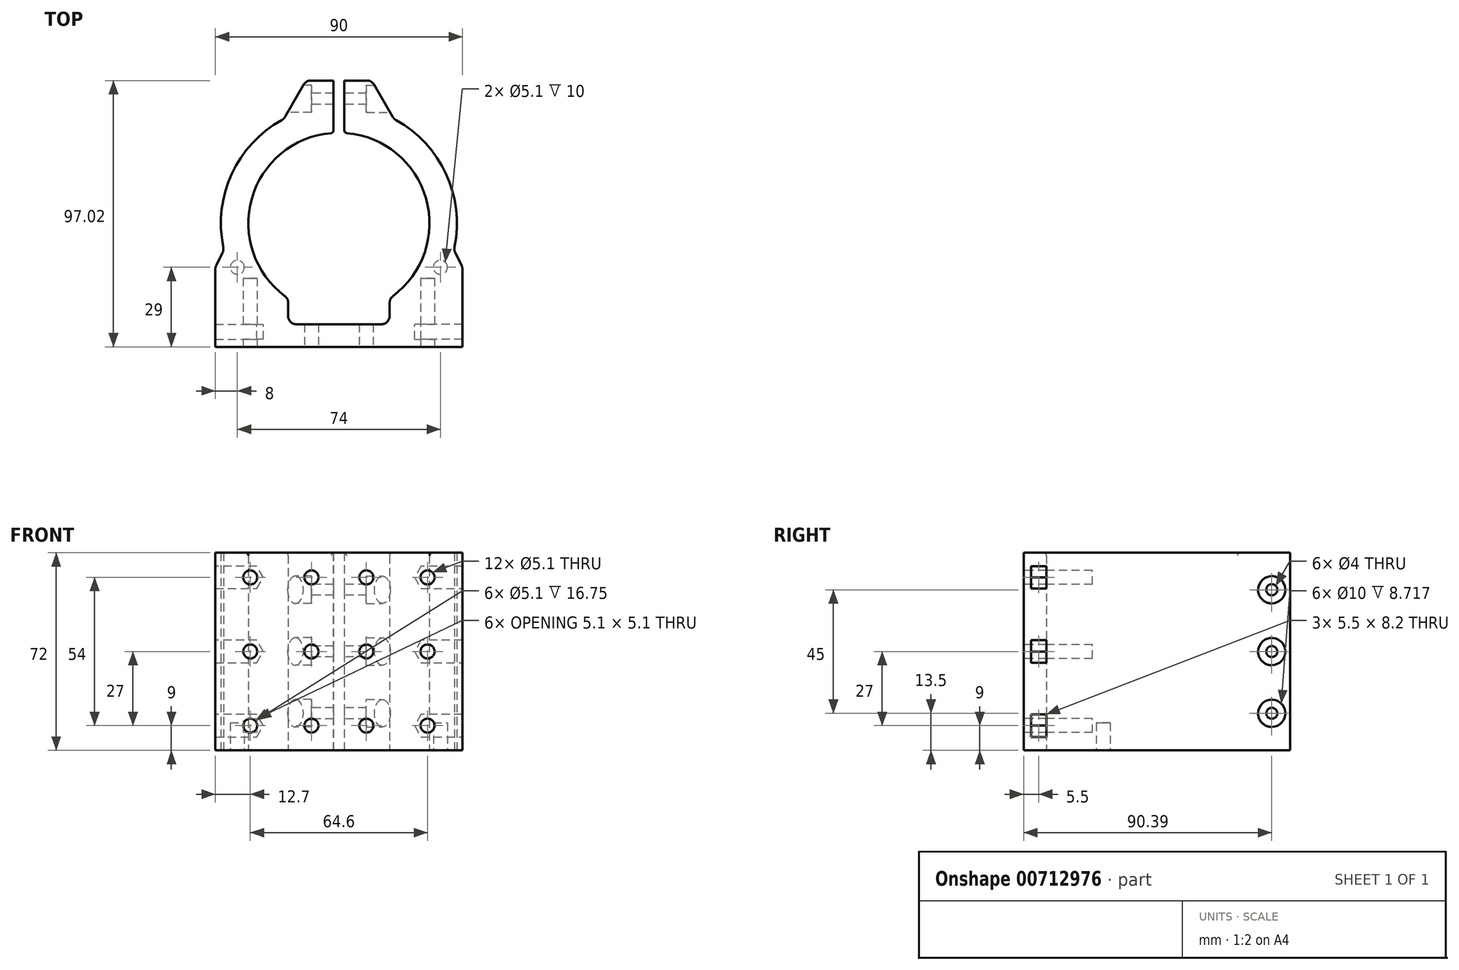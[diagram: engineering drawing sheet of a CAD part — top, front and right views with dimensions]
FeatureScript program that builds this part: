
annotation { "Feature Type Name" : "Feature", "Feature Type Description" : "" }
export const myFeature = defineFeature(function(context is Context, id is Id, definition is map)
    precondition{}
    {
        {
            var Q0;
            Q0=qCreatedBy(makeId("Top.planeOp"),FACE);
            var sketch = newSketch(context, id + "F0", { "sketchPlane" : qUnion([Q0])});
            skLineSegment(sketch, "E0", {"start": v(-45, -16) * mm, "end": v(-45, -45) * mm});
            skLineSegment(sketch, "E1", {"start": v(-45, -45) * mm, "end": v(45, -45) * mm});
            skLineSegment(sketch, "E2", {"start": v(45, -45) * mm, "end": v(45, -16) * mm});
            skLineSegment(sketch, "E3", {"start": v(45, -16) * mm, "end": v(41.9, -9.67) * mm});
            skLineSegment(sketch, "E4", {"start": v(-45, -16) * mm, "end": v(-41.9, -9.67) * mm});
            skLineSegment(sketch, "E5", {"start": v(-18.5, -27.33) * mm, "end": v(-18.5, -36.75) * mm});
            skLineSegment(sketch, "E6", {"start": v(-18.5, -36.75) * mm, "end": v(18.5, -36.75) * mm});
            skLineSegment(sketch, "E7", {"start": v(18.5, -36.75) * mm, "end": v(18.5, -27.33) * mm});
            skArc(sketch, "E8", {"start": v(-18.5, -27.33) * mm, "mid": v(-31.83, 8.71) * mm, "end": v(-2, 32.94) * mm});
            skArc(sketch, "E9", {"start": v(2, 32.94) * mm, "mid": v(31.83, 8.71) * mm, "end": v(18.5, -27.33) * mm});
            skArc(sketch, "E10", {"start": v(-41.9, -9.67) * mm, "mid": v(-39.1, 17.88) * mm, "end": v(-20.08, 38.02) * mm});
            skArc(sketch, "E11", {"start": v(20.08, 38.02) * mm, "mid": v(39.1, 17.88) * mm, "end": v(41.9, -9.67) * mm});
            skCircle(sketch, "E12", {"center": v(-37, -16) * mm, "radius": 2.55 * mm, "construction": true});
            skLineSegment(sketch, "E13", {"start": v(-37, -16) * mm, "end": v(-45, -16) * mm, "construction": true});
            skLineSegment(sketch, "E14", {"start": v(-37, -16) * mm, "end": v(-41.9, -9.67) * mm, "construction": true});
            skCircle(sketch, "E15", {"center": v(37, -16) * mm, "radius": 2.55 * mm, "construction": true});
            skLineSegment(sketch, "E16", {"start": v(37, -16) * mm, "end": v(41.9, -9.67) * mm, "construction": true});
            skLineSegment(sketch, "E17", {"start": v(37, -16) * mm, "end": v(45, -16) * mm, "construction": true});
            skLineSegment(sketch, "E18", {"start": v(-2, 32.94) * mm, "end": v(-2, 52.02) * mm});
            skLineSegment(sketch, "E19", {"start": v(2, 32.94) * mm, "end": v(2, 52.02) * mm});
            skLineSegment(sketch, "E20", {"start": v(2, 52.02) * mm, "end": v(12, 52.02) * mm});
            skLineSegment(sketch, "E21", {"start": v(12, 52.02) * mm, "end": v(20.08, 38.02) * mm});
            skLineSegment(sketch, "E22", {"start": v(-2, 52.02) * mm, "end": v(-12, 52.02) * mm});
            skLineSegment(sketch, "E23", {"start": v(-12, 52.02) * mm, "end": v(-20.08, 38.02) * mm});
            skLineSegment(sketch, "E24", {"start": v(-16.04, 45.02) * mm, "end": v(16.04, 45.02) * mm, "construction": true});
            skPoint(sketch, "E25", {"position": v(-2, 45.02) * mm});
            skSolve(sketch);
        }
        {
            var Q0;
            Q0 = qSketchRegion(id + "F0", true);
            extrude(context, id + "F1", {"entities" : qUnion([Q0]), "depth" : (18 * 4) * mm, "offsetDistance" : 25 * mm});
        }
        {
            var Q0;
            Q0=makeQuery(id+"F1.opExtrude","SWEPT_FACE",FACE,{"disambiguationData":[OSD([sQuery(id+"F0.wireOp",EDGE,"E1")])]});
            var sketch = newSketch(context, id + "F2", { "sketchPlane" : qUnion([Q0])});
            skCircle(sketch, "E26", {"center": v(-32.3, 9) * mm, "radius": 2.55 * mm});
            skCircle(sketch, "E27", {"center": v(-10, 9) * mm, "radius": 2.55 * mm});
            skCircle(sketch, "E28", {"center": v(10, 9) * mm, "radius": 2.55 * mm});
            skCircle(sketch, "E29", {"center": v(32.3, 9) * mm, "radius": 2.55 * mm});
            skCircle(sketch, "E30", {"center": v(32.3, 36) * mm, "radius": 2.55 * mm});
            skCircle(sketch, "E31", {"center": v(10, 36) * mm, "radius": 2.55 * mm});
            skCircle(sketch, "E32", {"center": v(-10, 36) * mm, "radius": 2.55 * mm});
            skCircle(sketch, "E33", {"center": v(-32.3, 36) * mm, "radius": 2.55 * mm});
            skCircle(sketch, "E34", {"center": v(-32.3, 63) * mm, "radius": 2.55 * mm});
            skCircle(sketch, "E35", {"center": v(-10, 63) * mm, "radius": 2.55 * mm});
            skCircle(sketch, "E36", {"center": v(10, 63) * mm, "radius": 2.55 * mm});
            skCircle(sketch, "E37", {"center": v(32.3, 63) * mm, "radius": 2.55 * mm});
            skLineSegment(sketch, "E38", {"start": v(-45, 9) * mm, "end": v(45, 9) * mm, "construction": true});
            skLineSegment(sketch, "E39", {"start": v(-45, 36) * mm, "end": v(45, 36) * mm, "construction": true});
            skLineSegment(sketch, "E40", {"start": v(-45, 63) * mm, "end": v(45, 63) * mm, "construction": true});
            skLineSegment(sketch, "E41", {"start": v(-32.3, 72) * mm, "end": v(-32.3, 0) * mm, "construction": true});
            skLineSegment(sketch, "E42", {"start": v(-10, 72) * mm, "end": v(-10, 0) * mm, "construction": true});
            skLineSegment(sketch, "E43", {"start": v(10, 72) * mm, "end": v(10, 0) * mm, "construction": true});
            skLineSegment(sketch, "E44", {"start": v(32.3, 72) * mm, "end": v(32.3, 0) * mm, "construction": true});
            skSolve(sketch);
        }
        {
            var Q0;
            Q0 = qSketchRegion(id + "F2", true);
            extrude(context, id + "F3", {"entities" : qUnion([Q0]), "operationType" : NewBodyOperationType.REMOVE, "oppositeDirection" : true, "depth" : 25 * mm, "offsetDistance" : 25 * mm});
        }
        {
            var Q0;
            Q0=makeQuery(id+"F1.opExtrude","CAP_FACE",FACE,{"disambiguationData":[OSD([sQuery(id+"F0.wireOp",EDGE,"E0"),sQuery(id+"F0.wireOp",EDGE,"E1"),sQuery(id+"F0.wireOp",EDGE,"E2"),sQuery(id+"F0.wireOp",EDGE,"E3"),sQuery(id+"F0.wireOp",EDGE,"E4"),sQuery(id+"F0.wireOp",EDGE,"E5"),sQuery(id+"F0.wireOp",EDGE,"E6"),sQuery(id+"F0.wireOp",EDGE,"E7"),sQuery(id+"F0.wireOp",EDGE,"E8"),sQuery(id+"F0.wireOp",EDGE,"E9"),sQuery(id+"F0.wireOp",EDGE,"E10"),sQuery(id+"F0.wireOp",EDGE,"E11"),sQuery(id+"F0.wireOp",EDGE,"E18"),sQuery(id+"F0.wireOp",EDGE,"E19"),sQuery(id+"F0.wireOp",EDGE,"E20"),sQuery(id+"F0.wireOp",EDGE,"E21"),sQuery(id+"F0.wireOp",EDGE,"E22"),sQuery(id+"F0.wireOp",EDGE,"E23")])],"isStart":true});
            var sketch = newSketch(context, id + "F4", { "sketchPlane" : qUnion([Q0])});
            skCircle(sketch, "E45", {"center": v(-37, 16) * mm, "radius": 2.55 * mm});
            skCircle(sketch, "E46", {"center": v(37, 16) * mm, "radius": 2.55 * mm});
            skSolve(sketch);
        }
        {
            var Q0;
            Q0 = qSketchRegion(id + "F4", true);
            extrude(context, id + "F5", {"entities" : qUnion([Q0]), "operationType" : NewBodyOperationType.REMOVE, "oppositeDirection" : true, "depth" : 10 * mm, "offsetDistance" : 25 * mm});
        }
        {
            var Q0;
            Q0=makeQuery(id+"F1.opExtrude","SWEPT_EDGE",EDGE,{"disambiguationData":[OSD([sQuery(id+"F0.wireOp",EDGE,"E7"),sQuery(id+"F0.wireOp",EDGE,"E9")])]});
            var Q1;
            Q1=makeQuery(id+"F1.opExtrude","SWEPT_EDGE",EDGE,{"disambiguationData":[OSD([sQuery(id+"F0.wireOp",EDGE,"E6"),sQuery(id+"F0.wireOp",EDGE,"E7")])]});
            var Q2;
            Q2=makeQuery(id+"F1.opExtrude","SWEPT_EDGE",EDGE,{"disambiguationData":[OSD([sQuery(id+"F0.wireOp",EDGE,"E5"),sQuery(id+"F0.wireOp",EDGE,"E8")])]});
            var Q3;
            Q3=makeQuery(id+"F1.opExtrude","SWEPT_EDGE",EDGE,{"disambiguationData":[OSD([sQuery(id+"F0.wireOp",EDGE,"E5"),sQuery(id+"F0.wireOp",EDGE,"E6")])]});
            fillet(context, id + "F6", {"entities" : qUnion([Q0, Q1, Q2, Q3]), "radius" : 3 * mm, "tangentPropagation" : true, "allowEdgeOverflow" : false});
        }
        {
            var Q0;
            Q0=makeQuery(id+"F1.opExtrude","SWEPT_EDGE",EDGE,{"disambiguationData":[OSD([sQuery(id+"F0.wireOp",EDGE,"E4"),sQuery(id+"F0.wireOp",EDGE,"E10")])]});
            var Q1;
            Q1=makeQuery(id+"F1.opExtrude","SWEPT_EDGE",EDGE,{"disambiguationData":[OSD([sQuery(id+"F0.wireOp",EDGE,"E0"),sQuery(id+"F0.wireOp",EDGE,"E4")])]});
            var Q2;
            Q2=makeQuery(id+"F1.opExtrude","SWEPT_EDGE",EDGE,{"disambiguationData":[OSD([sQuery(id+"F0.wireOp",EDGE,"E3"),sQuery(id+"F0.wireOp",EDGE,"E11")])]});
            var Q3;
            Q3=makeQuery(id+"F1.opExtrude","SWEPT_EDGE",EDGE,{"disambiguationData":[OSD([sQuery(id+"F0.wireOp",EDGE,"E2"),sQuery(id+"F0.wireOp",EDGE,"E3")])]});
            fillet(context, id + "F7", {"entities" : qUnion([Q0, Q1, Q2, Q3]), "radius" : 3 * mm, "tangentPropagation" : true, "allowEdgeOverflow" : false});
        }
        {
            var Q0;
            Q0=makeQuery(id+"F1.opExtrude","SWEPT_EDGE",EDGE,{"disambiguationData":[OSD([sQuery(id+"F0.wireOp",EDGE,"E10"),sQuery(id+"F0.wireOp",EDGE,"E23")])]});
            var Q1;
            Q1=makeQuery(id+"F1.opExtrude","SWEPT_EDGE",EDGE,{"disambiguationData":[OSD([sQuery(id+"F0.wireOp",EDGE,"E11"),sQuery(id+"F0.wireOp",EDGE,"E21")])]});
            fillet(context, id + "F8", {"entities" : qUnion([Q0, Q1]), "radius" : 3 * mm, "tangentPropagation" : true, "allowEdgeOverflow" : false});
        }
        {
            var Q0;
            Q0=qCreatedBy(makeId("Right.planeOp"),FACE);
            var sketch = newSketch(context, id + "F9", { "sketchPlane" : qUnion([Q0])});
            skLineSegment(sketch, "E47", {"start": v(52.02, 36) * mm, "end": v(-45, 36) * mm, "construction": true});
            skLineSegment(sketch, "E48", {"start": v(60.74, 58.5) * mm, "end": v(-53.65, 58.5) * mm, "construction": true});
            skLineSegment(sketch, "E49", {"start": v(60, 13.5) * mm, "end": v(-56.08, 13.5) * mm, "construction": true});
            skLineSegment(sketch, "E50", {"start": v(45.39, 72) * mm, "end": v(45.39, 0) * mm, "construction": true});
            skCircle(sketch, "E51", {"center": v(45.39, 58.5) * mm, "radius": 2 * mm});
            skCircle(sketch, "E52", {"center": v(45.39, 36) * mm, "radius": 2 * mm});
            skCircle(sketch, "E53", {"center": v(45.39, 13.5) * mm, "radius": 2 * mm});
            skSolve(sketch);
        }
        {
            var Q0;
            Q0 = qSketchRegion(id + "F9", true);
            extrude(context, id + "F10", {"entities" : qUnion([Q0]), "operationType" : NewBodyOperationType.REMOVE, "depth" : 25 * mm, "offsetDistance" : 25 * mm, "hasSecondDirection" : true, "secondDirectionOppositeDirection" : true, "secondDirectionDepth" : 25 * mm});
        }
        {
            var Q0;
            Q0=qCreatedBy(makeId("Right.planeOp"),FACE);
            cPlane(context, id + "F11", {"entities" : qUnion([Q0]), "cplaneType" : CPlaneType.OFFSET, "offset" : 25 * mm, "width" : 150 * mm, "height" : 150 * mm});
        }
        {
            var Q0;
            Q0=qCreatedBy(makeId("Right.planeOp"),FACE);
            cPlane(context, id + "F12", {"entities" : qUnion([Q0]), "cplaneType" : CPlaneType.OFFSET, "offset" : 25 * mm, "oppositeDirection" : true, "width" : 150 * mm, "height" : 150 * mm});
        }
        {
            var Q0;
            Q0=qCreatedBy(id+"F11.planeOp",FACE);
            var sketch = newSketch(context, id + "F13", { "sketchPlane" : qUnion([Q0])});
            skCircle(sketch, "E54.0", {"center": v(45.39, 58.5) * mm, "radius": 2 * mm, "construction": true});
            skCircle(sketch, "E55.0", {"center": v(45.39, 36) * mm, "radius": 2 * mm, "construction": true});
            skCircle(sketch, "E56.0", {"center": v(45.39, 13.5) * mm, "radius": 2 * mm, "construction": true});
            skCircle(sketch, "E57", {"center": v(45.39, 58.5) * mm, "radius": 5 * mm});
            skCircle(sketch, "E58", {"center": v(45.39, 36) * mm, "radius": 5 * mm});
            skCircle(sketch, "E59", {"center": v(45.39, 13.5) * mm, "radius": 5 * mm});
            skSolve(sketch);
        }
        {
            var Q0;
            Q0 = qSketchRegion(id + "F13", true);
            extrude(context, id + "F14", {"entities" : qUnion([Q0]), "operationType" : NewBodyOperationType.REMOVE, "oppositeDirection" : true, "depth" : 15 * mm, "offsetDistance" : 25 * mm});
        }
        {
            var Q0;
            Q0=qCreatedBy(id+"F12.planeOp",FACE);
            var sketch = newSketch(context, id + "F15", { "sketchPlane" : qUnion([Q0])});
            skCircle(sketch, "E60.0", {"center": v(45.39, 58.5) * mm, "radius": 2 * mm, "construction": true});
            skCircle(sketch, "E61.0", {"center": v(45.39, 36) * mm, "radius": 2 * mm, "construction": true});
            skCircle(sketch, "E62.0", {"center": v(45.39, 13.5) * mm, "radius": 2 * mm, "construction": true});
            skCircle(sketch, "E63", {"center": v(45.39, 58.5) * mm, "radius": 5 * mm});
            skCircle(sketch, "E64", {"center": v(45.39, 36) * mm, "radius": 5 * mm});
            skCircle(sketch, "E65", {"center": v(45.39, 13.5) * mm, "radius": 5 * mm});
            skSolve(sketch);
        }
        {
            var Q0;
            Q0=makeQuery(id+"F15.imprint","IMPRINT",FACE,{"disambiguationData":[TD([[makeQuery(id+"F15.imprint","IMPRINT",EDGE,{"derivedFrom":sQuery(id+"F15.wireOp",EDGE,"E63")}),1.0]])]});
            var Q1;
            Q1=makeQuery(id+"F15.imprint","IMPRINT",FACE,{"disambiguationData":[TD([[makeQuery(id+"F15.imprint","IMPRINT",EDGE,{"derivedFrom":sQuery(id+"F15.wireOp",EDGE,"E64")}),1.0]])]});
            var Q2;
            Q2=makeQuery(id+"F15.imprint","IMPRINT",FACE,{"disambiguationData":[TD([[makeQuery(id+"F15.imprint","IMPRINT",EDGE,{"derivedFrom":sQuery(id+"F15.wireOp",EDGE,"E65")}),1.0]])]});
            extrude(context, id + "F16", {"entities" : qUnion([Q0, Q1, Q2]), "operationType" : NewBodyOperationType.REMOVE, "depth" : 15 * mm, "offsetDistance" : 25 * mm});
        }
        {
            var Q0;
            Q0=makeQuery(id+"F1.opExtrude","SWEPT_FACE",FACE,{"disambiguationData":[OSD([sQuery(id+"F0.wireOp",EDGE,"E6")])]});
            var sketch = newSketch(context, id + "F17", { "sketchPlane" : qUnion([Q0])});
            skCircle(sketch, "E66.0", {"center": v(32.3, 63) * mm, "radius": 2.55 * mm, "construction": true});
            skCircle(sketch, "E67.0", {"center": v(32.3, 36) * mm, "radius": 2.55 * mm, "construction": true});
            skCircle(sketch, "E68.0", {"center": v(32.3, 9) * mm, "radius": 2.55 * mm, "construction": true});
            skCircle(sketch, "E69.0", {"center": v(-32.3, 9) * mm, "radius": 2.55 * mm, "construction": true});
            skCircle(sketch, "E70.0", {"center": v(-32.3, 36) * mm, "radius": 2.55 * mm, "construction": true});
            skCircle(sketch, "E71.0", {"center": v(-32.3, 63) * mm, "radius": 2.55 * mm, "construction": true});
            skCircle(sketch, "E72.cCircle", {"center": v(32.3, 36) * mm, "radius": 4.1 * mm, "construction": true});
            skLineSegment(sketch, "E72.0", {"start": v(29.93, 31.9) * mm, "end": v(27.57, 36) * mm});
            skLineSegment(sketch, "E72.1", {"start": v(27.57, 36) * mm, "end": v(29.93, 40.1) * mm});
            skLineSegment(sketch, "E72.2", {"start": v(29.93, 40.1) * mm, "end": v(34.67, 40.1) * mm});
            skLineSegment(sketch, "E72.3", {"start": v(34.67, 40.1) * mm, "end": v(37.03, 36) * mm, "construction": true});
            skLineSegment(sketch, "E72.4", {"start": v(37.03, 36) * mm, "end": v(34.67, 31.9) * mm, "construction": true});
            skLineSegment(sketch, "E72.5", {"start": v(34.67, 31.9) * mm, "end": v(29.93, 31.9) * mm});
            skPoint(sketch, "E72.0.midPoint", {"position": v(28.75, 33.95) * mm});
            skCircle(sketch, "E73.cCircle", {"center": v(32.3, 63) * mm, "radius": 4.1 * mm, "construction": true});
            skLineSegment(sketch, "E73.0", {"start": v(29.93, 58.9) * mm, "end": v(27.57, 63) * mm});
            skLineSegment(sketch, "E73.1", {"start": v(27.57, 63) * mm, "end": v(29.93, 67.1) * mm});
            skLineSegment(sketch, "E73.2", {"start": v(29.93, 67.1) * mm, "end": v(34.67, 67.1) * mm});
            skLineSegment(sketch, "E73.3", {"start": v(34.67, 67.1) * mm, "end": v(37.03, 63) * mm, "construction": true});
            skLineSegment(sketch, "E73.4", {"start": v(37.03, 63) * mm, "end": v(34.67, 58.9) * mm, "construction": true});
            skLineSegment(sketch, "E73.5", {"start": v(34.67, 58.9) * mm, "end": v(29.93, 58.9) * mm});
            skPoint(sketch, "E73.0.midPoint", {"position": v(28.75, 60.95) * mm});
            skCircle(sketch, "E74.cCircle", {"center": v(32.3, 9) * mm, "radius": 4.1 * mm, "construction": true});
            skLineSegment(sketch, "E74.0", {"start": v(29.93, 4.9) * mm, "end": v(27.57, 9) * mm});
            skLineSegment(sketch, "E74.1", {"start": v(27.57, 9) * mm, "end": v(29.93, 13.1) * mm});
            skLineSegment(sketch, "E74.2", {"start": v(29.93, 13.1) * mm, "end": v(34.67, 13.1) * mm});
            skLineSegment(sketch, "E74.3", {"start": v(34.67, 13.1) * mm, "end": v(37.03, 9) * mm, "construction": true});
            skLineSegment(sketch, "E74.4", {"start": v(37.03, 9) * mm, "end": v(34.67, 4.9) * mm, "construction": true});
            skLineSegment(sketch, "E74.5", {"start": v(34.67, 4.9) * mm, "end": v(29.93, 4.9) * mm});
            skPoint(sketch, "E74.0.midPoint", {"position": v(28.75, 6.95) * mm});
            skCircle(sketch, "E75.cCircle", {"center": v(-32.3, 9) * mm, "radius": 4.1 * mm, "construction": true});
            skLineSegment(sketch, "E75.0", {"start": v(-34.67, 4.9) * mm, "end": v(-37.03, 9) * mm, "construction": true});
            skLineSegment(sketch, "E75.1", {"start": v(-37.03, 9) * mm, "end": v(-34.67, 13.1) * mm, "construction": true});
            skLineSegment(sketch, "E75.2", {"start": v(-34.67, 13.1) * mm, "end": v(-29.93, 13.1) * mm});
            skLineSegment(sketch, "E75.3", {"start": v(-29.93, 13.1) * mm, "end": v(-27.57, 9) * mm});
            skLineSegment(sketch, "E75.4", {"start": v(-27.57, 9) * mm, "end": v(-29.93, 4.9) * mm});
            skLineSegment(sketch, "E75.5", {"start": v(-29.93, 4.9) * mm, "end": v(-34.67, 4.9) * mm});
            skPoint(sketch, "E75.0.midPoint", {"position": v(-35.85, 6.95) * mm});
            skCircle(sketch, "E76.cCircle", {"center": v(-32.3, 36) * mm, "radius": 4.1 * mm, "construction": true});
            skPoint(sketch, "E76.cCircle.perimeterSnap0", {"position": v(-35.85, 11.05) * mm});
            skLineSegment(sketch, "E76.0", {"start": v(-34.67, 31.9) * mm, "end": v(-37.03, 36) * mm, "construction": true});
            skLineSegment(sketch, "E76.1", {"start": v(-37.03, 36) * mm, "end": v(-34.67, 40.1) * mm, "construction": true});
            skLineSegment(sketch, "E76.2", {"start": v(-34.67, 40.1) * mm, "end": v(-29.93, 40.1) * mm});
            skLineSegment(sketch, "E76.3", {"start": v(-29.93, 40.1) * mm, "end": v(-27.57, 36) * mm});
            skLineSegment(sketch, "E76.4", {"start": v(-27.57, 36) * mm, "end": v(-29.93, 31.9) * mm});
            skLineSegment(sketch, "E76.5", {"start": v(-29.93, 31.9) * mm, "end": v(-34.67, 31.9) * mm});
            skPoint(sketch, "E76.0.midPoint", {"position": v(-35.85, 33.95) * mm});
            skPoint(sketch, "E76.0.midPoint.positionSnap0", {"position": v(-35.85, 11.05) * mm});
            skCircle(sketch, "E77.cCircle", {"center": v(-32.3, 63) * mm, "radius": 4.1 * mm, "construction": true});
            skLineSegment(sketch, "E77.0", {"start": v(-34.67, 58.9) * mm, "end": v(-37.03, 63) * mm, "construction": true});
            skLineSegment(sketch, "E77.1", {"start": v(-37.03, 63) * mm, "end": v(-34.67, 67.1) * mm, "construction": true});
            skLineSegment(sketch, "E77.2", {"start": v(-34.67, 67.1) * mm, "end": v(-29.93, 67.1) * mm});
            skLineSegment(sketch, "E77.3", {"start": v(-29.93, 67.1) * mm, "end": v(-27.57, 63) * mm});
            skLineSegment(sketch, "E77.4", {"start": v(-27.57, 63) * mm, "end": v(-29.93, 58.9) * mm});
            skLineSegment(sketch, "E77.5", {"start": v(-29.93, 58.9) * mm, "end": v(-34.67, 58.9) * mm});
            skPoint(sketch, "E77.0.midPoint", {"position": v(-35.85, 60.95) * mm});
            skLineSegment(sketch, "E78", {"start": v(34.67, 13.1) * mm, "end": v(54.8, 13.1) * mm});
            skLineSegment(sketch, "E79", {"start": v(34.67, 4.9) * mm, "end": v(54.8, 4.9) * mm});
            skLineSegment(sketch, "E80", {"start": v(54.8, 13.1) * mm, "end": v(54.8, 4.9) * mm});
            skLineSegment(sketch, "E81", {"start": v(34.67, 67.1) * mm, "end": v(54.8, 67.1) * mm});
            skLineSegment(sketch, "E82", {"start": v(54.8, 67.1) * mm, "end": v(54.8, 58.9) * mm});
            skLineSegment(sketch, "E83", {"start": v(34.67, 58.9) * mm, "end": v(54.8, 58.9) * mm});
            skLineSegment(sketch, "E84", {"start": v(34.67, 40.1) * mm, "end": v(54.8, 40.1) * mm});
            skLineSegment(sketch, "E85", {"start": v(34.67, 31.9) * mm, "end": v(54.8, 31.9) * mm});
            skLineSegment(sketch, "E86.trimOffspring", {"start": v(54.8, 40.1) * mm, "end": v(54.8, 31.9) * mm});
            skLineSegment(sketch, "E87", {"start": v(-55.13, 67.1) * mm, "end": v(-55.13, 58.9) * mm});
            skLineSegment(sketch, "E88", {"start": v(-34.67, 67.1) * mm, "end": v(-55.13, 67.1) * mm});
            skLineSegment(sketch, "E89", {"start": v(-34.67, 58.9) * mm, "end": v(-55.13, 58.9) * mm});
            skLineSegment(sketch, "E90", {"start": v(-34.67, 40.1) * mm, "end": v(-55.13, 40.1) * mm});
            skLineSegment(sketch, "E91", {"start": v(-34.67, 31.9) * mm, "end": v(-55.13, 31.9) * mm});
            skLineSegment(sketch, "E92", {"start": v(-34.67, 13.1) * mm, "end": v(-55.13, 13.1) * mm});
            skLineSegment(sketch, "E93", {"start": v(-34.67, 4.9) * mm, "end": v(-55.13, 4.9) * mm});
            skLineSegment(sketch, "E94.trimOffspring", {"start": v(-55.13, 13.1) * mm, "end": v(-55.13, 4.9) * mm});
            skPoint(sketch, "E95.orphan", {"position": v(-55.13, 0) * mm});
            skLineSegment(sketch, "E96.trimOffspring", {"start": v(-55.13, 40.1) * mm, "end": v(-55.13, 31.9) * mm});
            skSolve(sketch);
        }
        {
            var Q0;
            Q0 = qSketchRegion(id + "F17", true);
            extrude(context, id + "F18", {"entities" : qUnion([Q0]), "operationType" : NewBodyOperationType.REMOVE, "oppositeDirection" : true, "depth" : 5.5 * mm, "offsetDistance" : 25 * mm});
        }
        {
            var Q0;
            Q0=makeQuery(id+"F1.opExtrude","SWEPT_EDGE",EDGE,{"disambiguationData":[OSD([sQuery(id+"F0.wireOp",EDGE,"E22"),sQuery(id+"F0.wireOp",EDGE,"E23")])]});
            var Q1;
            Q1=makeQuery(id+"F1.opExtrude","SWEPT_EDGE",EDGE,{"disambiguationData":[OSD([sQuery(id+"F0.wireOp",EDGE,"E20"),sQuery(id+"F0.wireOp",EDGE,"E21")])]});
            fillet(context, id + "F19", {"entities" : qUnion([Q0, Q1]), "radius" : 3 * mm, "tangentPropagation" : true, "allowEdgeOverflow" : false});
        }
        {
            var Q0;
            Q0=makeQuery(id+"F1.opExtrude","SWEPT_EDGE",EDGE,{"disambiguationData":[OSD([sQuery(id+"F0.wireOp",EDGE,"E9"),sQuery(id+"F0.wireOp",EDGE,"E19")])]});
            var Q1;
            Q1=makeQuery(id+"F1.opExtrude","SWEPT_EDGE",EDGE,{"disambiguationData":[OSD([sQuery(id+"F0.wireOp",EDGE,"E8"),sQuery(id+"F0.wireOp",EDGE,"E18")])]});
            var Q2;
            Q2=makeQuery(id+"F1.opExtrude","CAP_EDGE",EDGE,{"disambiguationData":[OSD([sQuery(id+"F0.wireOp",EDGE,"E9")])],"isStart":false});
            fillet(context, id + "F20", {"entities" : qUnion([Q0, Q1, Q2]), "radius" : 1 * mm, "tangentPropagation" : true, "allowEdgeOverflow" : false});
        }
    });
